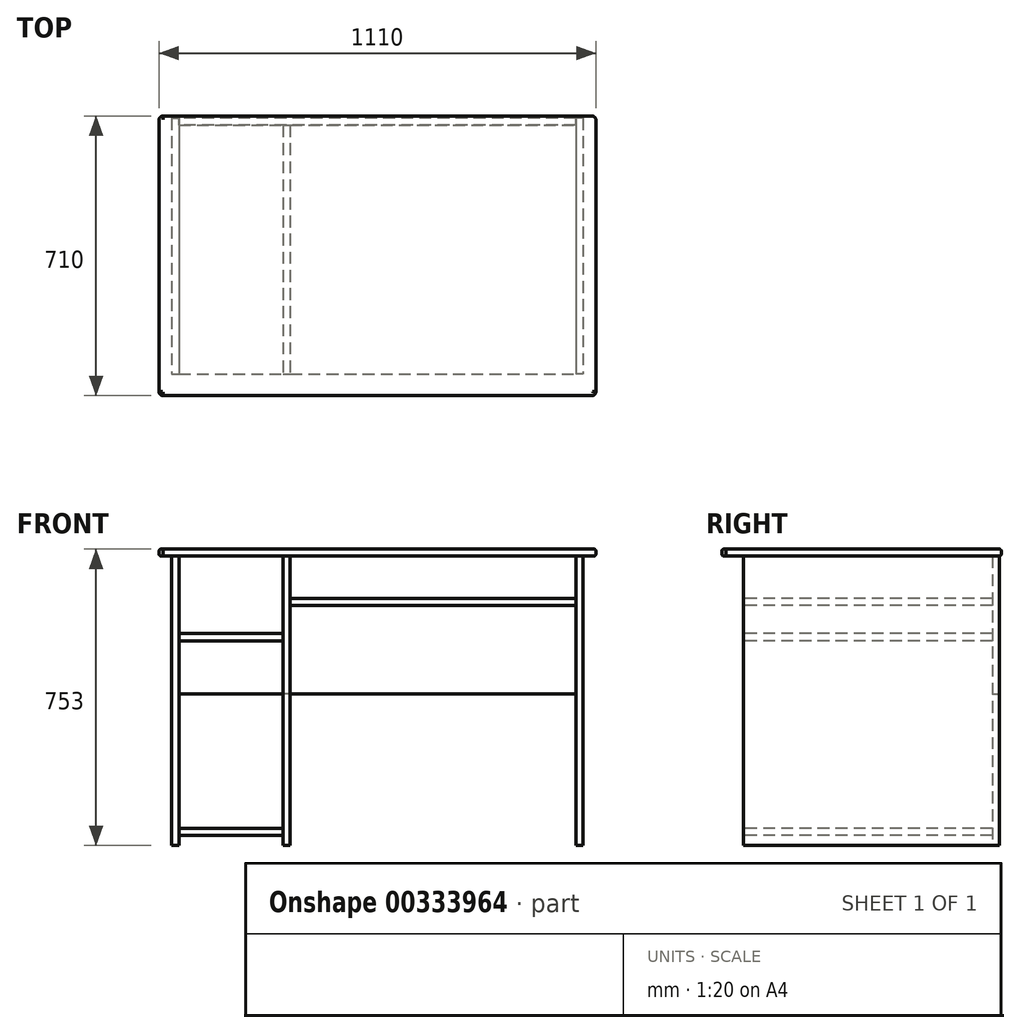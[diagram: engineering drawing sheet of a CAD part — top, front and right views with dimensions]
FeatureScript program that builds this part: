
annotation { "Feature Type Name" : "Feature", "Feature Type Description" : "" }
export const myFeature = defineFeature(function(context is Context, id is Id, definition is map)
    precondition{}
    {
        {
            var Q0;
            Q0=qCreatedBy(makeId("Front.planeOp"),FACE);
            var sketch = newSketch(context, id + "F0", { "sketchPlane" : qUnion([Q0])});
            skLineSegment(sketch, "E0.bottom", {"start": v(-301, 735) * mm, "end": v(-283, 735) * mm});
            skLineSegment(sketch, "E0.top", {"start": v(-301, 0) * mm, "end": v(-283, 0) * mm});
            skLineSegment(sketch, "E0.left", {"start": v(-301, 735) * mm, "end": v(-301, 0) * mm});
            skLineSegment(sketch, "E0.right", {"start": v(-283, 735) * mm, "end": v(-283, 0) * mm});
            skLineSegment(sketch, "E1.bottom", {"start": v(-18, 735) * mm, "end": v(0, 735) * mm});
            skLineSegment(sketch, "E1.top", {"start": v(-18, 0) * mm, "end": v(0, 0) * mm});
            skLineSegment(sketch, "E1.left", {"start": v(-18, 735) * mm, "end": v(-18, 0) * mm});
            skLineSegment(sketch, "E1.right", {"start": v(0, 735) * mm, "end": v(0, 0) * mm});
            skLineSegment(sketch, "E2.bottom", {"start": v(744, 735) * mm, "end": v(726, 735) * mm});
            skLineSegment(sketch, "E2.top", {"start": v(744, 0) * mm, "end": v(726, 0) * mm});
            skLineSegment(sketch, "E2.left", {"start": v(744, 735) * mm, "end": v(744, 0) * mm});
            skLineSegment(sketch, "E2.right", {"start": v(726, 735) * mm, "end": v(726, 0) * mm});
            skLineSegment(sketch, "E3.bottom", {"start": v(-283, 43) * mm, "end": v(-18, 43) * mm});
            skLineSegment(sketch, "E3.top", {"start": v(-283, 25) * mm, "end": v(-18, 25) * mm});
            skLineSegment(sketch, "E3.left", {"start": v(-283, 43) * mm, "end": v(-283, 25) * mm});
            skLineSegment(sketch, "E3.right", {"start": v(-18, 43) * mm, "end": v(-18, 25) * mm});
            skLineSegment(sketch, "E4.bottom", {"start": v(0, 628) * mm, "end": v(726, 628) * mm});
            skLineSegment(sketch, "E4.top", {"start": v(0, 610) * mm, "end": v(726, 610) * mm});
            skLineSegment(sketch, "E4.left", {"start": v(0, 628) * mm, "end": v(0, 610) * mm});
            skLineSegment(sketch, "E4.right", {"start": v(726, 628) * mm, "end": v(726, 610) * mm});
            skLineSegment(sketch, "E5.bottom", {"start": v(-283, 538) * mm, "end": v(-18, 538) * mm});
            skLineSegment(sketch, "E5.top", {"start": v(-283, 520) * mm, "end": v(-18, 520) * mm});
            skLineSegment(sketch, "E5.left", {"start": v(-283, 538) * mm, "end": v(-283, 520) * mm});
            skLineSegment(sketch, "E5.right", {"start": v(-18, 538) * mm, "end": v(-18, 520) * mm});
            skSolve(sketch);
        }
        {
            var Q0;
            {var subQ1=sQuery(id+"F0.wireOp",EDGE,"E0.bottom");Q0=makeQuery(id+"F0.imprint","IMPRINT",FACE,{"disambiguationData":[TD([[makeQuery(id+"F0.imprint","IMPRINT",EDGE,{"derivedFrom":subQ1}),-1.0]])]});}
            extrude(context, id + "F1", {"entities" : qUnion([Q0]), "oppositeDirection" : true, "depth" : 650 * mm});
        }
        {
            var Q0;
            {var subQ1=sQuery(id+"F0.wireOp",EDGE,"E2.bottom");Q0=makeQuery(id+"F0.imprint","IMPRINT",FACE,{"disambiguationData":[TD([[makeQuery(id+"F0.imprint","IMPRINT",EDGE,{"derivedFrom":subQ1}),1.0]])]});}
            extrude(context, id + "F2", {"entities" : qUnion([Q0]), "oppositeDirection" : true, "depth" : 650 * mm});
        }
        {
            var Q0;
            Q0=makeQuery(id+"F2.opExtrude","CAP_FACE",FACE,{"disambiguationData":[OSD([sQuery(id+"F0.wireOp",EDGE,"E2.bottom"),sQuery(id+"F0.wireOp",EDGE,"E2.top"),sQuery(id+"F0.wireOp",EDGE,"E2.left"),sQuery(id+"F0.wireOp",EDGE,"E2.right"),sQuery(id+"F0.wireOp",EDGE,"E4.right")])],"isStart":false});
            var sketch = newSketch(context, id + "F3", { "sketchPlane" : qUnion([Q0])});
            skLineSegment(sketch, "E6.bottom", {"start": v(-726, 735) * mm, "end": v(283, 735) * mm});
            skLineSegment(sketch, "E6.top", {"start": v(-726, 385) * mm, "end": v(283, 385) * mm});
            skLineSegment(sketch, "E6.left", {"start": v(-726, 735) * mm, "end": v(-726, 385) * mm});
            skLineSegment(sketch, "E6.right", {"start": v(283, 735) * mm, "end": v(283, 385) * mm});
            skSolve(sketch);
        }
        {
            var Q0;
            {var subQ3=sQuery(id+"F3.wireOp",EDGE,"E6.left");Q0=makeQuery(id+"F3.imprint","IMPRINT",FACE,{"disambiguationData":[TD([[makeQuery(id+"F3.imprint","IMPRINT",EDGE,{"derivedFrom":subQ3}),1.0]])]});}
            var Q1;
            {var subQ0=sQuery(id+"F3.wireOp",EDGE,"E6.bottom");var subQ1=makeQuery(id+"F5.opExtrude","CAP_EDGE",EDGE,{"disambiguationData":[OSD([sQuery(id+"F0.wireOp",EDGE,"E1.left"),sQuery(id+"F0.wireOp",EDGE,"E3.right"),sQuery(id+"F0.wireOp",EDGE,"E5.right")])],"isStart":false});var subQ2=makeQuery(id+"F3.imprint","INTERSECT",VERTEX,{"derivedFrom":[subQ1,subQ0]});var subQ3=makeQuery(id+"F5.opExtrude","CAP_EDGE",EDGE,{"disambiguationData":[OSD([sQuery(id+"F0.wireOp",EDGE,"E1.right"),sQuery(id+"F0.wireOp",EDGE,"E4.left")])],"isStart":false});var subQ4=makeQuery(id+"F3.imprint","INTERSECT",VERTEX,{"derivedFrom":[subQ3,subQ0]});Q1=makeQuery(id+"F3.imprint","IMPRINT",FACE,{"disambiguationData":[TD([[makeQuery(id+"F3.imprint","IMPRINT",EDGE,{"disambiguationData":[TD([[subQ2,-1.0],[subQ4,1.0]])],"derivedFrom":subQ0}),1.0]])]});}
            var Q2;
            {var subQ3=sQuery(id+"F3.wireOp",EDGE,"E6.right");Q2=makeQuery(id+"F3.imprint","IMPRINT",FACE,{"disambiguationData":[TD([[makeQuery(id+"F3.imprint","IMPRINT",EDGE,{"derivedFrom":subQ3}),-1.0]])]});}
            extrude(context, id + "F4", {"entities" : qUnion([Q0, Q1, Q2]), "oppositeDirection" : true, "depth" : 18 * mm});
        }
        {
            var Q0;
            {var subQ3=sQuery(id+"F0.wireOp",EDGE,"E1.bottom");Q0=makeQuery(id+"F0.imprint","IMPRINT",FACE,{"disambiguationData":[TD([[makeQuery(id+"F0.imprint","IMPRINT",EDGE,{"derivedFrom":subQ3}),-1.0]])]});}
            var Q1;
            Q1=makeQuery(id+"F4.opExtrude","CAP_FACE",FACE,{"disambiguationData":[OSD([sQuery(id+"F3.wireOp",EDGE,"E6.bottom"),sQuery(id+"F3.wireOp",EDGE,"E6.top"),sQuery(id+"F3.wireOp",EDGE,"E6.left"),sQuery(id+"F3.wireOp",EDGE,"E6.right")])],"isStart":false});
            extrude(context, id + "F5", {"entities" : qUnion([Q0]), "endBound" : BoundingType.UP_TO_SURFACE, "oppositeDirection" : true, "endBoundEntityFace" : qUnion([Q1]), "depth" : 650 * mm});
        }
        {
            var Q0;
            Q0=makeQuery(id+"F0.imprint","IMPRINT",FACE,{"disambiguationData":[TD([[makeQuery(id+"F0.imprint","IMPRINT",EDGE,{"derivedFrom":sQuery(id+"F0.wireOp",EDGE,"E5.bottom")}),-1.0]])]});
            var Q1;
            Q1=makeQuery(id+"F4.opExtrude","CAP_FACE",FACE,{"disambiguationData":[OSD([sQuery(id+"F3.wireOp",EDGE,"E6.bottom"),sQuery(id+"F3.wireOp",EDGE,"E6.top"),sQuery(id+"F3.wireOp",EDGE,"E6.left"),sQuery(id+"F3.wireOp",EDGE,"E6.right")])],"isStart":false});
            extrude(context, id + "F6", {"entities" : qUnion([Q0]), "endBound" : BoundingType.UP_TO_SURFACE, "oppositeDirection" : true, "endBoundEntityFace" : qUnion([Q1]), "depth" : 650 * mm});
        }
        {
            var Q0;
            Q0=makeQuery(id+"F0.imprint","IMPRINT",FACE,{"disambiguationData":[TD([[makeQuery(id+"F0.imprint","IMPRINT",EDGE,{"derivedFrom":sQuery(id+"F0.wireOp",EDGE,"E3.bottom")}),-1.0]])]});
            var Q1;
            Q1=makeQuery(id+"F4.opExtrude","CAP_FACE",FACE,{"disambiguationData":[OSD([sQuery(id+"F3.wireOp",EDGE,"E6.bottom"),sQuery(id+"F3.wireOp",EDGE,"E6.top"),sQuery(id+"F3.wireOp",EDGE,"E6.left"),sQuery(id+"F3.wireOp",EDGE,"E6.right")])],"isStart":false});
            extrude(context, id + "F7", {"entities" : qUnion([Q0]), "endBound" : BoundingType.UP_TO_SURFACE, "oppositeDirection" : true, "endBoundEntityFace" : qUnion([Q1]), "depth" : 650 * mm});
        }
        {
            var Q0;
            Q0=makeQuery(id+"F0.imprint","IMPRINT",FACE,{"disambiguationData":[TD([[makeQuery(id+"F0.imprint","IMPRINT",EDGE,{"derivedFrom":sQuery(id+"F0.wireOp",EDGE,"E4.bottom")}),-1.0]])]});
            var Q1;
            Q1=makeQuery(id+"F4.opExtrude","CAP_FACE",FACE,{"disambiguationData":[OSD([sQuery(id+"F3.wireOp",EDGE,"E6.bottom"),sQuery(id+"F3.wireOp",EDGE,"E6.top"),sQuery(id+"F3.wireOp",EDGE,"E6.left"),sQuery(id+"F3.wireOp",EDGE,"E6.right")])],"isStart":false});
            extrude(context, id + "F8", {"entities" : qUnion([Q0]), "endBound" : BoundingType.UP_TO_SURFACE, "oppositeDirection" : true, "endBoundEntityFace" : qUnion([Q1]), "depth" : 650 * mm});
        }
        {
            var Q0;
            Q0=makeQuery(id+"F1.opExtrude","SWEPT_FACE",FACE,{"disambiguationData":[OSD([sQuery(id+"F0.wireOp",EDGE,"E0.bottom")])]});
            var sketch = newSketch(context, id + "F9", { "sketchPlane" : qUnion([Q0])});
            skLineSegment(sketch, "E7.bottom", {"start": v(-323.5, 655) * mm, "end": v(766.5, 655) * mm});
            skLineSegment(sketch, "E7.top", {"start": v(-323.5, -55) * mm, "end": v(766.5, -55) * mm});
            skLineSegment(sketch, "E7.left", {"start": v(-333.5, 645) * mm, "end": v(-333.5, -45) * mm});
            skLineSegment(sketch, "E7.right", {"start": v(776.5, 645) * mm, "end": v(776.5, -45) * mm});
            skLineSegment(sketch, "E8", {"start": v(744, 325) * mm, "end": v(-301, 325) * mm, "construction": true});
            skLineSegment(sketch, "E9", {"start": v(221.5, -55) * mm, "end": v(221.5, 655) * mm, "construction": true});
            skPoint(sketch, "E10", {"position": v(221.5, 325) * mm});
            skPoint(sketch, "E11.visualSharp", {"position": v(-333.5, 655) * mm});
            skArc(sketch, "E11.filletArc", {"start": v(-323.5, 655) * mm, "mid": v(-330.57, 652.07) * mm, "end": v(-333.5, 645) * mm});
            skPoint(sketch, "E12.visualSharp", {"position": v(-333.5, -55) * mm});
            skArc(sketch, "E12.filletArc", {"start": v(-333.5, -45) * mm, "mid": v(-330.57, -52.07) * mm, "end": v(-323.5, -55) * mm});
            skPoint(sketch, "E13.visualSharp", {"position": v(776.5, -55) * mm});
            skArc(sketch, "E13.filletArc", {"start": v(766.5, -55) * mm, "mid": v(773.57, -52.07) * mm, "end": v(776.5, -45) * mm});
            skPoint(sketch, "E14.visualSharp", {"position": v(776.5, 655) * mm});
            skArc(sketch, "E14.filletArc", {"start": v(776.5, 645) * mm, "mid": v(773.57, 652.07) * mm, "end": v(766.5, 655) * mm});
            skSolve(sketch);
        }
        {
            var Q0;
            Q0=makeQuery(id+"F9.imprint","IMPRINT",FACE,{"disambiguationData":[TD([[makeQuery(id+"F9.imprint","IMPRINT",EDGE,{"derivedFrom":sQuery(id+"F9.wireOp",EDGE,"E7.bottom")}),-1.0]])]});
            var Q1;
            {var subQ0=sQuery(id+"F0.wireOp",EDGE,"E0.bottom");Q1=makeQuery(id+"F9.imprint","IMPRINT",FACE,{"disambiguationData":[TD([[makeQuery(id+"F9.imprint","IMPRINT",EDGE,{"derivedFrom":makeQuery(id+"F1.opExtrude","CAP_EDGE",EDGE,{"disambiguationData":[OSD([subQ0])],"isStart":true})}),1.0]])]});}
            extrude(context, id + "F10", {"entities" : qUnion([Q0, Q1]), "depth" : 18 * mm});
        }
        {
            var Q0;
            Q0=makeQuery(id+"F10.opExtrude","CAP_EDGE",EDGE,{"disambiguationData":[OSD([sQuery(id+"F9.wireOp",EDGE,"E7.top")])],"isStart":true});
            var Q1;
            Q1=makeQuery(id+"F10.opExtrude","CAP_EDGE",EDGE,{"disambiguationData":[OSD([sQuery(id+"F9.wireOp",EDGE,"E7.top")])],"isStart":false});
            fillet(context, id + "F11", {"entities" : qUnion([Q0, Q1]), "radius" : 9 * mm, "tangentPropagation" : true, "rho" : 0.65, "crossSection" : FilletCrossSection.CONIC, "allowEdgeOverflow" : false});
        }
    });
